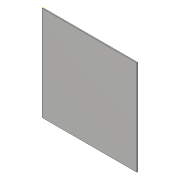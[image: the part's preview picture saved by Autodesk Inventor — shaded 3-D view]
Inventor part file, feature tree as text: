
AUTODESK INVENTOR PART (.ipt)
format: ipt  version: 2018 (Build 220112000, 112)  size: 83,968 bytes
history: native  units: in
note: dims shown in document units (in); Inventor stores cm internally (conversion verified against a paired STEP export)
features: sketch x2, direct_edit x1, move_body x1
ambient origin geometry x8: Origin, YZ Plane, XZ Plane, XY Plane, X Axis, Y Axis, Z Axis, Center Point
bodies: Solid1 (feature_tree), Body1 (feature_tree)
feature tree (4):
  sketch  "Sketch1"  dims[d0=0.0in d1=0.0in d2=-0.3937in]
  direct_edit  "Direct Edit1"
  sketch  "Sketch2"
  move_body  "Move1"
